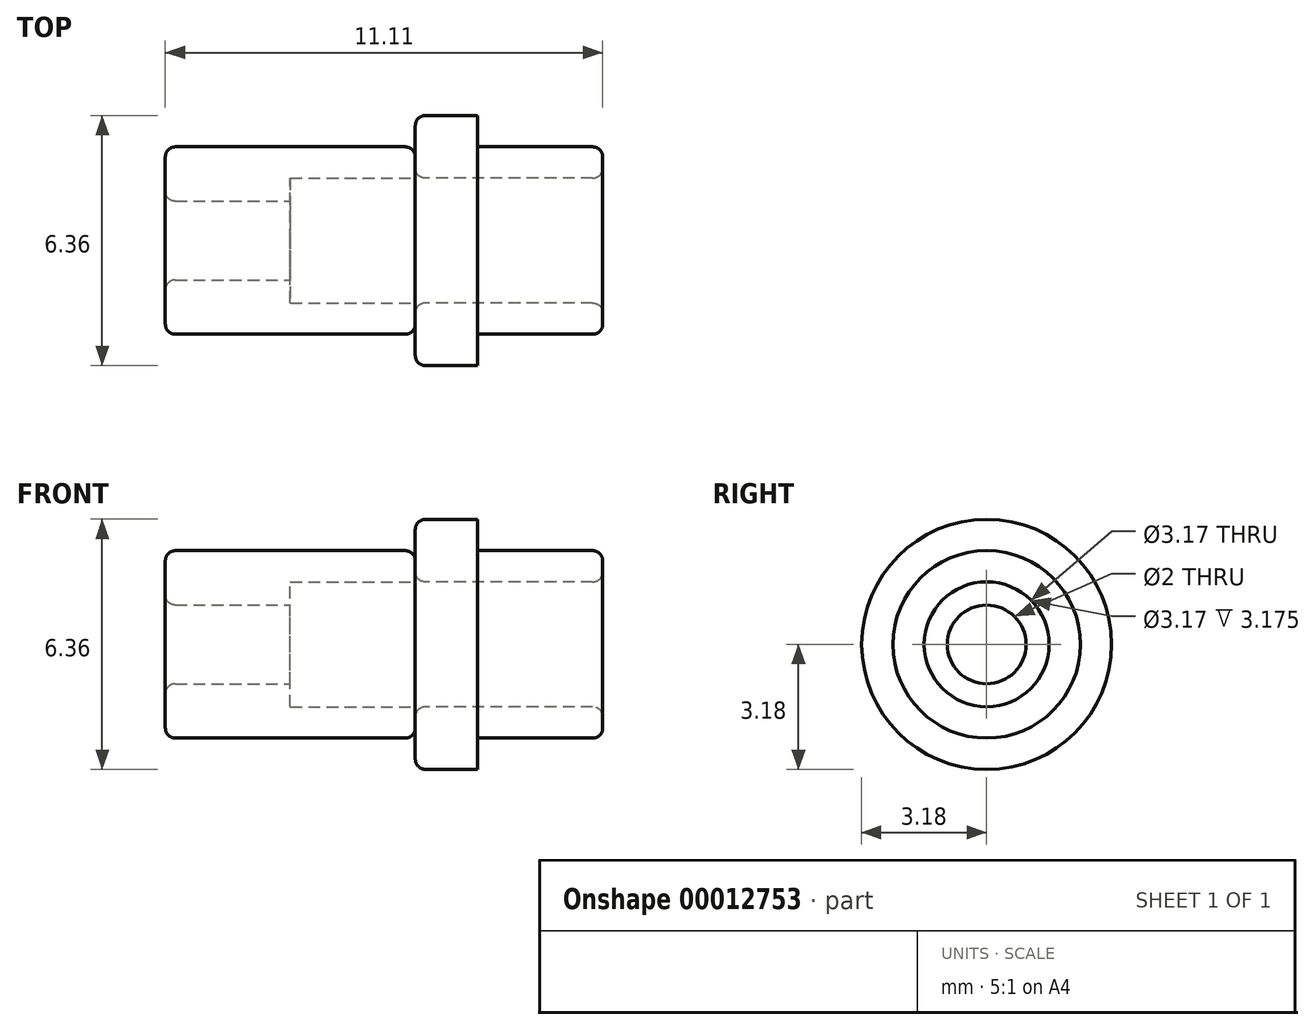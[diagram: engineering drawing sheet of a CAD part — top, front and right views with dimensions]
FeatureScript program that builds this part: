
annotation { "Feature Type Name" : "Feature", "Feature Type Description" : "" }
export const myFeature = defineFeature(function(context is Context, id is Id, definition is map)
    precondition{}
    {
        {
            var Q0;
            Q0=qCreatedBy(makeId("Right.planeOp"),FACE);
            var sketch = newSketch(context, id + "F0", { "sketchPlane" : qUnion([Q0])});
            skCircle(sketch, "E0", {"center": v(0, 0) * mm, "radius": 3.18 * mm});
            skCircle(sketch, "E1", {"center": v(0, 0) * mm, "radius": 1.59 * mm});
            skCircle(sketch, "E2", {"center": v(0, 0) * mm, "radius": 2.38 * mm});
            skSolve(sketch);
        }
        {
            var Q0;
            Q0=makeQuery(id+"F0.imprint","IMPRINT",FACE,{"disambiguationData":[TD([[makeQuery(id+"F0.imprint","IMPRINT",EDGE,{"derivedFrom":sQuery(id+"F0.wireOp",EDGE,"E0")}),1.0]])]});
            extrude(context, id + "F1", {"entities" : qUnion([Q0]), "depth" : 1.59 * mm});
        }
        {
            var Q0;
            Q0=makeQuery(id+"F0.imprint","IMPRINT",FACE,{"disambiguationData":[TD([[makeQuery(id+"F0.imprint","IMPRINT",EDGE,{"derivedFrom":sQuery(id+"F0.wireOp",EDGE,"E1")}),-1.0]])]});
            extrude(context, id + "F2", {"entities" : qUnion([Q0]), "operationType" : NewBodyOperationType.ADD, "depth" : 4.76 * mm});
        }
        {
            var Q0;
            Q0=makeQuery(id+"F1.opExtrude","CAP_EDGE",EDGE,{"disambiguationData":[OSD([sQuery(id+"F0.wireOp",EDGE,"E0")])],"isStart":true});
            var Q1;
            Q1=makeQuery(id+"F2.opExtrude","CAP_EDGE",EDGE,{"disambiguationData":[OSD([sQuery(id+"F0.wireOp",EDGE,"E1")])],"isStart":true});
            var Q2;
            Q2=makeQuery(id+"F2.opExtrude","CAP_EDGE",EDGE,{"disambiguationData":[OSD([sQuery(id+"F0.wireOp",EDGE,"E1")])],"isStart":false});
            var Q3;
            Q3=makeQuery(id+"F2.opExtrude","CAP_EDGE",EDGE,{"disambiguationData":[OSD([sQuery(id+"F0.wireOp",EDGE,"E2")])],"isStart":false});
            fillet(context, id + "F3", {"entities" : qUnion([Q0, Q1, Q2, Q3]), "radius" : 0.25 * mm, "tangentPropagation" : true, "allowEdgeOverflow" : false});
        }
        {
            var Q0;
            Q0=qCreatedBy(makeId("Right.planeOp"),FACE);
            var sketch = newSketch(context, id + "F4", { "sketchPlane" : qUnion([Q0])});
            skCircle(sketch, "E3", {"center": v(0, 0) * mm, "radius": 3.18 * mm});
            skCircle(sketch, "E4", {"center": v(0, 0) * mm, "radius": 2.38 * mm});
            skCircle(sketch, "E5", {"center": v(0, 0) * mm, "radius": 1.59 * mm});
            skSolve(sketch);
        }
        {
            var Q0;
            Q0=makeQuery(id+"F4.imprint","IMPRINT",FACE,{"disambiguationData":[TD([[makeQuery(id+"F4.imprint","IMPRINT",EDGE,{"derivedFrom":sQuery(id+"F4.wireOp",EDGE,"E4")}),1.0]])]});
            extrude(context, id + "F5", {"entities" : qUnion([Q0]), "depth" : 3.97 * mm});
        }
        {
            var Q0;
            Q0=makeQuery(id+"F4.imprint","IMPRINT",FACE,{"disambiguationData":[TD([[makeQuery(id+"F4.imprint","IMPRINT",EDGE,{"derivedFrom":sQuery(id+"F4.wireOp",EDGE,"E3")}),1.0]])]});
            extrude(context, id + "F6", {"entities" : qUnion([Q0]), "operationType" : NewBodyOperationType.ADD, "depth" : 0.8 * mm});
        }
        {
            var Q0;
            Q0=makeQuery(id+"F5.opExtrude","CAP_EDGE",EDGE,{"disambiguationData":[OSD([sQuery(id+"F4.wireOp",EDGE,"E4")])],"isStart":false});
            var Q1;
            Q1=makeQuery(id+"F5.opExtrude","CAP_EDGE",EDGE,{"disambiguationData":[OSD([sQuery(id+"F4.wireOp",EDGE,"E5")])],"isStart":false});
            var Q2;
            Q2=makeQuery(id+"F5.opExtrude","CAP_EDGE",EDGE,{"disambiguationData":[OSD([sQuery(id+"F4.wireOp",EDGE,"E5")])],"isStart":true});
            var Q3;
            Q3=makeQuery(id+"F6.opExtrude","CAP_EDGE",EDGE,{"disambiguationData":[OSD([sQuery(id+"F4.wireOp",EDGE,"E3")])],"isStart":true});
            fillet(context, id + "F7", {"entities" : qUnion([Q0, Q1, Q2, Q3]), "radius" : 0.25 * mm, "tangentPropagation" : true, "allowEdgeOverflow" : false});
        }
        {
            var Q0;
            Q0=qCreatedBy(makeId("Right.planeOp"),FACE);
            var sketch = newSketch(context, id + "F8", { "sketchPlane" : qUnion([Q0])});
            skCircle(sketch, "E6", {"center": v(0, 0) * mm, "radius": 2.38 * mm});
            skCircle(sketch, "E7", {"center": v(0, 0) * mm, "radius": 1.59 * mm});
            skCircle(sketch, "E8", {"center": v(0, 0) * mm, "radius": 1 * mm});
            skSolve(sketch);
        }
        {
            var Q0;
            Q0=makeQuery(id+"F8.imprint","IMPRINT",FACE,{"disambiguationData":[TD([[makeQuery(id+"F8.imprint","IMPRINT",EDGE,{"derivedFrom":sQuery(id+"F8.wireOp",EDGE,"E7")}),1.0]])]});
            var Q1;
            Q1=makeQuery(id+"F8.imprint","IMPRINT",FACE,{"disambiguationData":[TD([[makeQuery(id+"F8.imprint","IMPRINT",EDGE,{"derivedFrom":sQuery(id+"F8.wireOp",EDGE,"E6")}),1.0]])]});
            extrude(context, id + "F9", {"entities" : qUnion([Q0, Q1]), "oppositeDirection" : true, "depth" : 6.35 * mm});
        }
        {
            var Q0;
            Q0=makeQuery(id+"F8.imprint","IMPRINT",FACE,{"disambiguationData":[TD([[makeQuery(id+"F8.imprint","IMPRINT",EDGE,{"derivedFrom":sQuery(id+"F8.wireOp",EDGE,"E7")}),1.0]])]});
            extrude(context, id + "F10", {"entities" : qUnion([Q0]), "operationType" : NewBodyOperationType.REMOVE, "oppositeDirection" : true, "depth" : 3.17 * mm});
        }
        {
            var Q0;
            Q0=makeQuery(id+"F9.opExtrude","CAP_EDGE",EDGE,{"disambiguationData":[OSD([sQuery(id+"F8.wireOp",EDGE,"E6")])],"isStart":true});
            var Q1;
            Q1=makeQuery(id+"F10.boolean.opBoolean","COPY",EDGE,{"derivedFrom":makeQuery(id+"F10.opExtrude","CAP_EDGE",EDGE,{"disambiguationData":[OSD([sQuery(id+"F8.wireOp",EDGE,"E7")])],"isStart":true})});
            var Q2;
            Q2=makeQuery(id+"F9.opExtrude","CAP_EDGE",EDGE,{"disambiguationData":[OSD([sQuery(id+"F8.wireOp",EDGE,"E8")])],"isStart":false});
            var Q3;
            Q3=makeQuery(id+"F9.opExtrude","CAP_EDGE",EDGE,{"disambiguationData":[OSD([sQuery(id+"F8.wireOp",EDGE,"E6")])],"isStart":false});
            fillet(context, id + "F11", {"entities" : qUnion([Q0, Q1, Q2, Q3]), "radius" : 0.25 * mm, "tangentPropagation" : true, "allowEdgeOverflow" : false});
        }
    });
